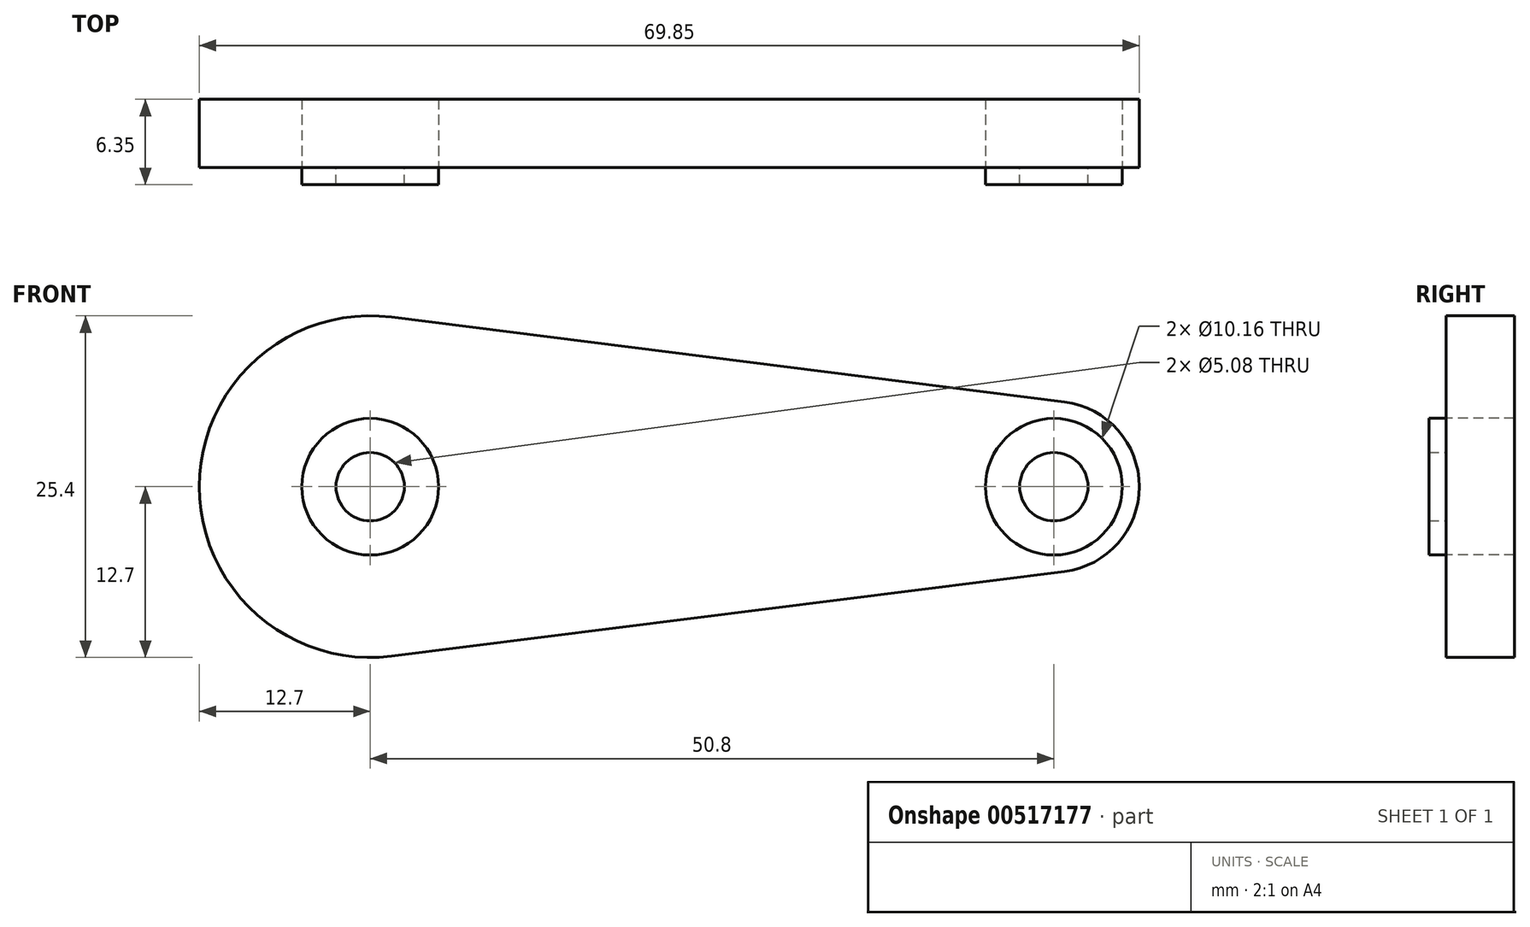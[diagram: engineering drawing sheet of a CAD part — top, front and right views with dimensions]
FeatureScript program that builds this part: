
annotation { "Feature Type Name" : "Feature", "Feature Type Description" : "" }
export const myFeature = defineFeature(function(context is Context, id is Id, definition is map)
    precondition{}
    {
        {
            var Q0;
            Q0=qCreatedBy(makeId("Front.planeOp"),FACE);
            var sketch = newSketch(context, id + "F0", { "sketchPlane" : qUnion([Q0])});
            skLineSegment(sketch, "E0", {"start": v(-25.4, 0) * mm, "end": v(25.4, 0) * mm});
            skPoint(sketch, "E1", {"position": v(0, 0) * mm});
            skCircle(sketch, "E2", {"center": v(-25.4, 0) * mm, "radius": 12.7 * mm});
            skCircle(sketch, "E3", {"center": v(25.4, 0) * mm, "radius": 6.35 * mm});
            skLineSegment(sketch, "E4", {"start": v(26.2, 6.3) * mm, "end": v(-23.81, 12.6) * mm});
            skLineSegment(sketch, "E5", {"start": v(26.2, -6.3) * mm, "end": v(-23.81, -12.6) * mm});
            skCircle(sketch, "E6", {"center": v(-25.4, 0) * mm, "radius": 2.54 * mm});
            skCircle(sketch, "E7", {"center": v(-25.4, 0) * mm, "radius": 0.6 * mm});
            skCircle(sketch, "E8", {"center": v(25.4, 0) * mm, "radius": 2.54 * mm});
            skCircle(sketch, "E9.0", {"center": v(-25.4, 0) * mm, "radius": 5.08 * mm});
            skCircle(sketch, "E10.0", {"center": v(25.4, 0) * mm, "radius": 5.08 * mm});
            skSolve(sketch);
        }
        {
            var Q0;
            Q0=makeQuery(id+"F0.imprint","IMPRINT",FACE,{"disambiguationData":[TD([[makeQuery(id+"F0.imprint","IMPRINT",EDGE,{"derivedFrom":sQuery(id+"F0.wireOp",EDGE,"E8")}),-1.0]])]});
            var Q1;
            Q1=makeQuery(id+"F0.imprint","IMPRINT",FACE,{"disambiguationData":[TD([[makeQuery(id+"F0.imprint","IMPRINT",EDGE,{"derivedFrom":sQuery(id+"F0.wireOp",EDGE,"E6")}),-1.0]])]});
            extrude(context, id + "F1", {"entities" : qUnion([Q0, Q1]), "depth" : 1.27 * mm, "offsetDistance" : 25.4 * mm});
        }
        {
            var Q0;
            Q0=makeQuery(id+"F0.imprint","IMPRINT",FACE,{"disambiguationData":[TD([[makeQuery(id+"F0.imprint","IMPRINT",EDGE,{"derivedFrom":sQuery(id+"F0.wireOp",EDGE,"E9.0")}),-1.0]])]});
            var Q1;
            {var subQ5=sQuery(id+"F0.wireOp",EDGE,"E4");Q1=makeQuery(id+"F0.imprint","IMPRINT",FACE,{"disambiguationData":[TD([[makeQuery(id+"F0.imprint","IMPRINT",EDGE,{"derivedFrom":subQ5}),1.0]])]});}
            var Q2;
            {var subQ5=sQuery(id+"F0.wireOp",EDGE,"E5");Q2=makeQuery(id+"F0.imprint","IMPRINT",FACE,{"disambiguationData":[TD([[makeQuery(id+"F0.imprint","IMPRINT",EDGE,{"derivedFrom":subQ5}),-1.0]])]});}
            var Q3;
            Q3=makeQuery(id+"F0.imprint","IMPRINT",FACE,{"disambiguationData":[TD([[makeQuery(id+"F0.imprint","IMPRINT",EDGE,{"derivedFrom":sQuery(id+"F0.wireOp",EDGE,"E10.0")}),-1.0]])]});
            extrude(context, id + "F2", {"entities" : qUnion([Q0, Q1, Q2, Q3]), "oppositeDirection" : true, "depth" : 5.08 * mm, "offsetDistance" : 25.4 * mm});
        }
    });
